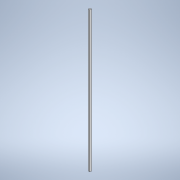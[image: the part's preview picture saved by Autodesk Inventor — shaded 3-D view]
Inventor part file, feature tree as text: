
AUTODESK INVENTOR PART (.ipt)
format: ipt  version: 2022 (Build 260153000, 153)  size: 149,504 bytes
history: native  units: mm
features: extrude x1, sketch x1
ambient origin geometry x8: Origin, YZ Plane, XZ Plane, XY Plane, X Axis, Y Axis, Z Axis, Center Point
bodies: Body1 (feature_tree)
feature tree (2):
  extrude  "Extrusion7"  Depth=5.0mm
  sketch  "Sketch4"  dims[d31=34.456mm d103=5.0mm d104=5.0mm d105=476.0mm d106=0.0mm]
